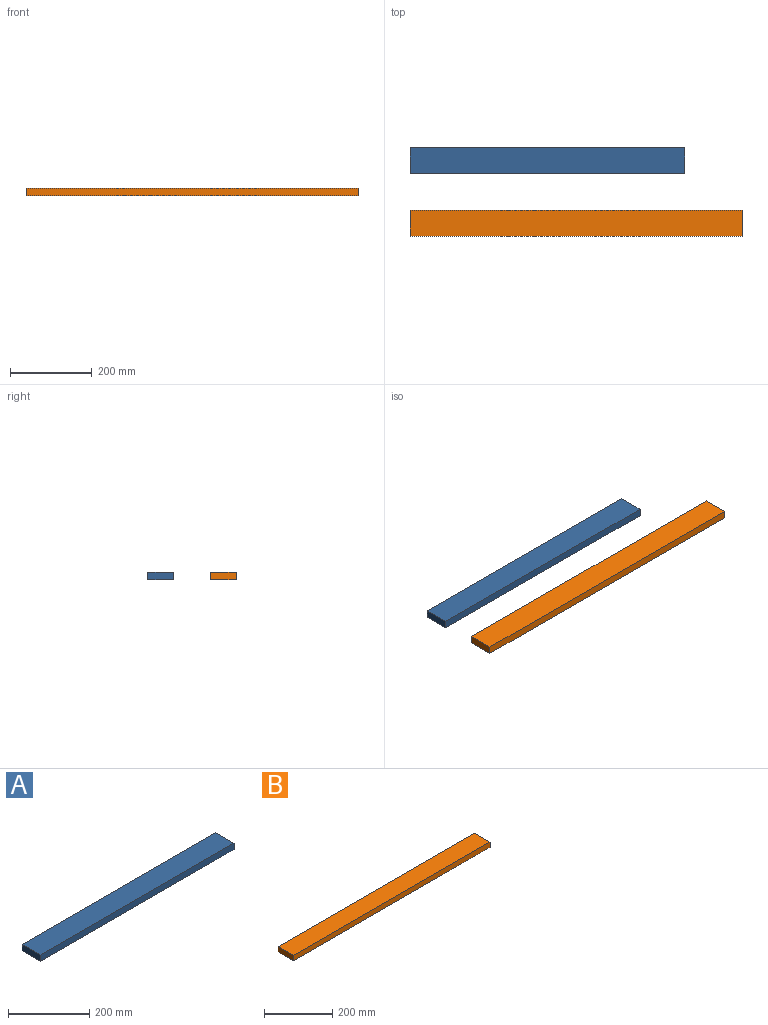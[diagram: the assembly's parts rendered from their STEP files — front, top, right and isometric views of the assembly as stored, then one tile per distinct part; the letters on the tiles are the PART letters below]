
ASSEMBLY  parts=2 mates=1
PART A: 6 faces, bbox 673.1x63.5x19.1 mm
  f0: plane 63.5x19.05mm, normal (-1,0,0), area 1209.7mm2, adj f1,f3,f4,f5
  f1: plane 673.1x19.05mm, normal (0,-1,0), area 12822.6mm2, adj f0,f2,f4,f5
  f2: plane 63.5x19.05mm, normal (1,0,0), area 1209.7mm2, adj f1,f3,f4,f5
  f3: plane 673.1x19.05mm, normal (0,1,0), area 12822.6mm2, adj f0,f2,f4,f5
  f4: plane 673.1x63.5mm, normal (0,0,1), area 42741.9mm2, adj f0,f1,f2,f3
  f5: plane 673.1x63.5mm, normal (0,0,-1), area 42741.9mm2, adj f0,f1,f2,f3
PART B: 6 faces, bbox 812.8x63.5x19.1 mm
  f0: plane 63.5x19.05mm, normal (-1,0,0), area 1209.7mm2, adj f1,f3,f4,f5
  f1: plane 812.8x19.05mm, normal (0,-1,0), area 15483.8mm2, adj f0,f2,f4,f5
  f2: plane 63.5x19.05mm, normal (1,0,0), area 1209.7mm2, adj f1,f3,f4,f5
  f3: plane 812.8x19.05mm, normal (0,1,0), area 15483.8mm2, adj f0,f2,f4,f5
  f4: plane 812.8x63.5mm, normal (0,0,1), area 51612.8mm2, adj f0,f1,f2,f3
  f5: plane 812.8x63.5mm, normal (0,0,-1), area 51612.8mm2, adj f0,f1,f2,f3
PLACE A t=(-68.31,30.93,0)mm
PLACE B t=(38.52,0,0)mm
MATE slider A.f1 <-> B.f3  axis (0,-1,0) through (-383.72,28.08,19.05)mm
